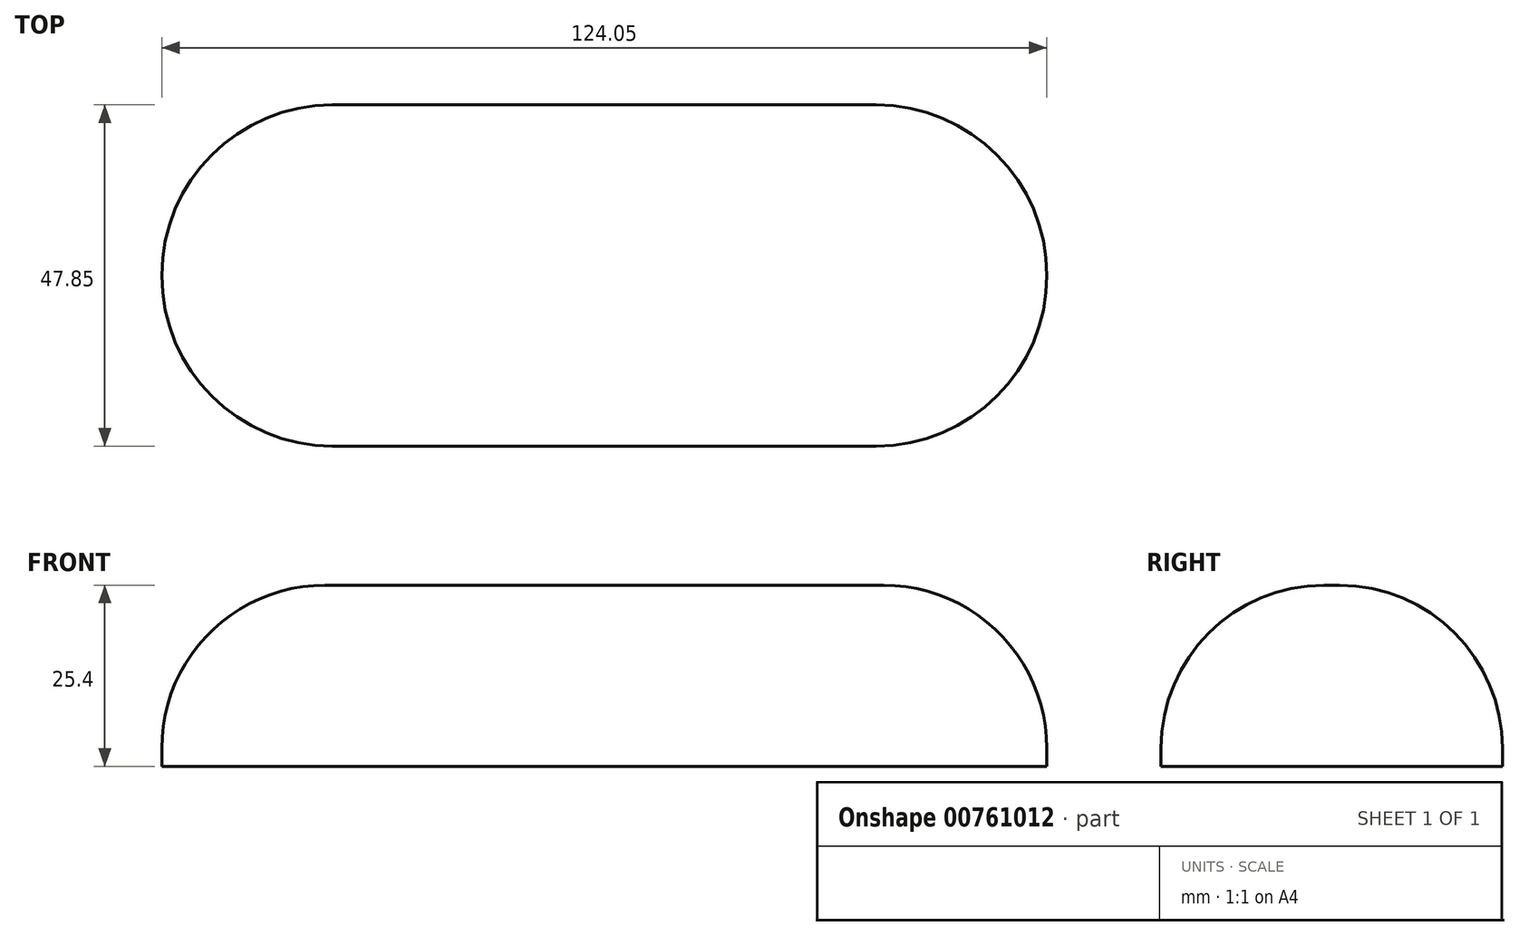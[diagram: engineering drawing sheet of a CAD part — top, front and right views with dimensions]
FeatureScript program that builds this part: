
annotation { "Feature Type Name" : "Feature", "Feature Type Description" : "" }
export const myFeature = defineFeature(function(context is Context, id is Id, definition is map)
    precondition{}
    {
        {
            var Q0;
            Q0=qCreatedBy(makeId("Top.planeOp"),FACE);
            var sketch = newSketch(context, id + "F0", { "sketchPlane" : qUnion([Q0])});
            skLineSegment(sketch, "E0.bottom", {"start": v(-31.97, 19.64) * mm, "end": v(44.23, 19.64) * mm});
            skLineSegment(sketch, "E0.top", {"start": v(-31.97, -28.2) * mm, "end": v(44.23, -28.2) * mm});
            skLineSegment(sketch, "E0.left", {"start": v(-31.97, 19.64) * mm, "end": v(-31.97, -28.2) * mm});
            skLineSegment(sketch, "E0.right", {"start": v(44.23, 19.64) * mm, "end": v(44.23, -28.2) * mm});
            skArc(sketch, "E1", {"start": v(44.23, -28.2) * mm, "mid": v(68.16, -4.28) * mm, "end": v(44.23, 19.64) * mm});
            skArc(sketch, "E2", {"start": v(-31.97, 19.64) * mm, "mid": v(-55.9, -4.28) * mm, "end": v(-31.97, -28.2) * mm});
            skSolve(sketch);
        }
        {
            var Q0;
            Q0=makeQuery(id+"F0.imprint","IMPRINT",FACE,{"disambiguationData":[TD([[makeQuery(id+"F0.imprint","IMPRINT",EDGE,{"derivedFrom":sQuery(id+"F0.wireOp",EDGE,"E0.bottom")}),-1.0]])]});
            var Q1;
            Q1=makeQuery(id+"F0.imprint","IMPRINT",FACE,{"disambiguationData":[TD([[makeQuery(id+"F0.imprint","IMPRINT",EDGE,{"derivedFrom":sQuery(id+"F0.wireOp",EDGE,"E0.left")}),-1.0]])]});
            var Q2;
            Q2=makeQuery(id+"F0.imprint","IMPRINT",FACE,{"disambiguationData":[TD([[makeQuery(id+"F0.imprint","IMPRINT",EDGE,{"derivedFrom":sQuery(id+"F0.wireOp",EDGE,"E0.right")}),1.0]])]});
            extrude(context, id + "F1", {"entities" : qUnion([Q0, Q1, Q2]), "depth" : 25.4 * mm, "offsetDistance" : 25.4 * mm});
        }
        {
            var Q0;
            Q0=makeQuery(id+"F1.opExtrude","CAP_FACE",FACE,{"disambiguationData":[OSD([sQuery(id+"F0.wireOp",EDGE,"E0.bottom"),sQuery(id+"F0.wireOp",EDGE,"E0.top"),sQuery(id+"F0.wireOp",EDGE,"E1"),sQuery(id+"F0.wireOp",EDGE,"E2")])],"isStart":false});
            fillet(context, id + "F2", {"entities" : qUnion([Q0]), "radius" : 22.86 * mm, "tangentPropagation" : true, "allowEdgeOverflow" : false});
        }
    });
